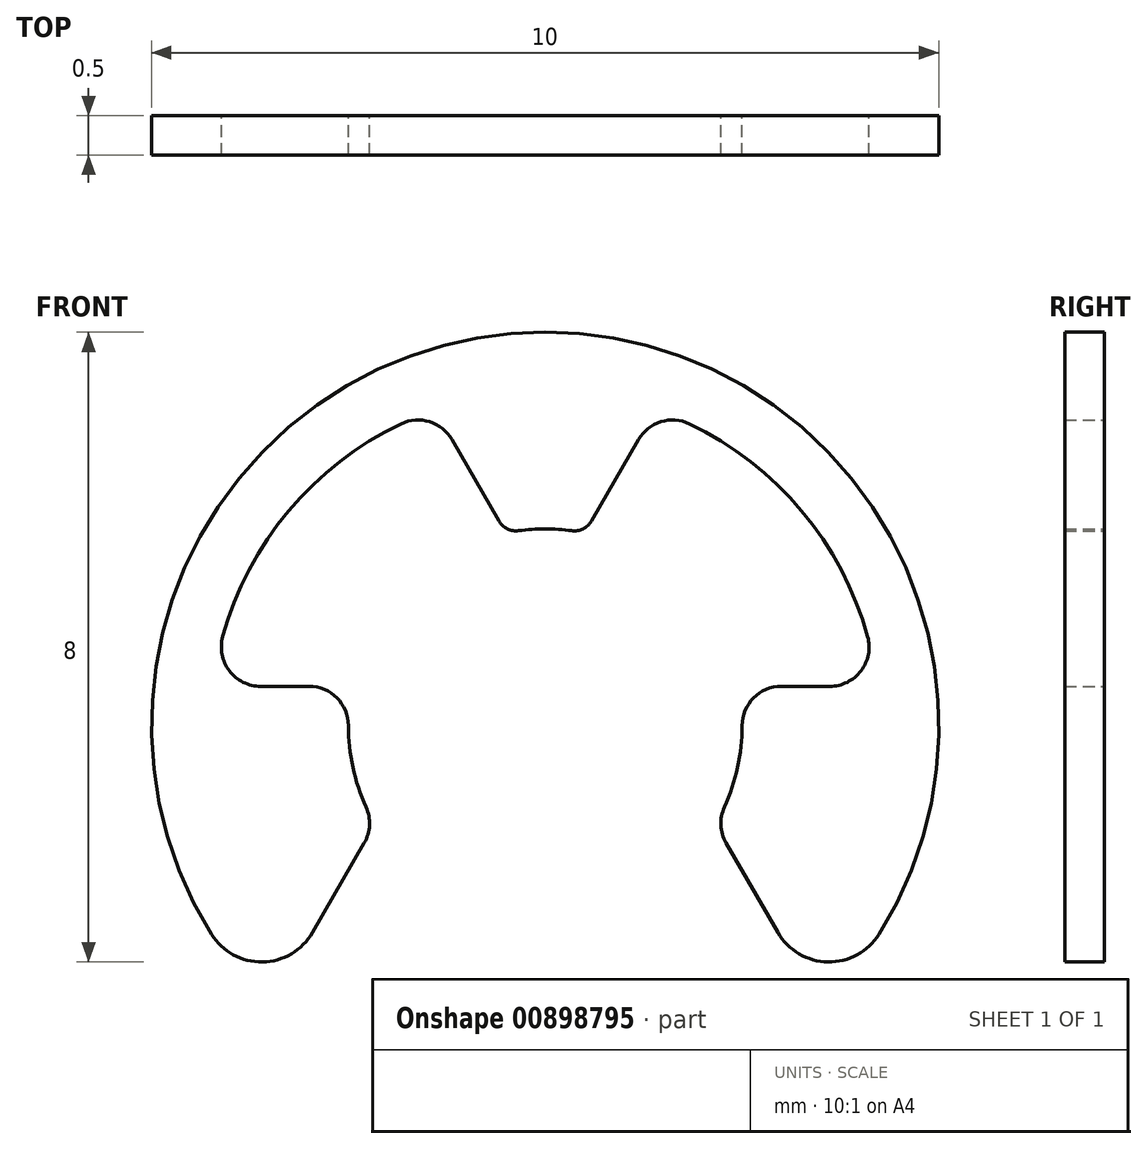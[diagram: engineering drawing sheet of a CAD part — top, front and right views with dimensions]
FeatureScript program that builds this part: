
annotation { "Feature Type Name" : "Feature", "Feature Type Description" : "" }
export const myFeature = defineFeature(function(context is Context, id is Id, definition is map)
    precondition{}
    {
        {
            var Q0;
            Q0=qCreatedBy(makeId("Front.planeOp"),FACE);
            var sketch = newSketch(context, id + "F0", { "sketchPlane" : qUnion([Q0])});
            skArc(sketch, "E0", {"start": v(4.24, -2.65) * mm, "mid": v(0, 5) * mm, "end": v(-4.24, -2.65) * mm});
            skArc(sketch, "E1", {"start": v(4.1, 1.13) * mm, "mid": v(3.26, 2.73) * mm, "end": v(1.83, 3.83) * mm});
            skArc(sketch, "E2", {"start": v(2.28, -1.03) * mm, "mid": v(2.44, -0.53) * mm, "end": v(2.5, 0) * mm});
            skLineSegment(sketch, "E3", {"start": v(-2.95, -2.63) * mm, "end": v(-2.3, -1.5) * mm});
            skLineSegment(sketch, "E4", {"start": v(2.95, -2.63) * mm, "end": v(2.3, -1.5) * mm});
            skLineSegment(sketch, "E5", {"start": v(3, 0.5) * mm, "end": v(3.61, 0.5) * mm});
            skLineSegment(sketch, "E6", {"start": v(-3, 0.5) * mm, "end": v(-3.61, 0.5) * mm});
            skLineSegment(sketch, "E7", {"start": v(-1.18, 3.63) * mm, "end": v(-0.59, 2.6) * mm});
            skLineSegment(sketch, "E8", {"start": v(0.59, 2.6) * mm, "end": v(1.18, 3.63) * mm});
            skArc(sketch, "E9.trimOffspring", {"start": v(-2.5, 0) * mm, "mid": v(-2.44, -0.53) * mm, "end": v(-2.28, -1.03) * mm});
            skArc(sketch, "E10.trimOffspring", {"start": v(0.34, 2.48) * mm, "mid": v(0, 2.5) * mm, "end": v(-0.34, 2.48) * mm});
            skArc(sketch, "E11.trimOffspring", {"start": v(-1.83, 3.83) * mm, "mid": v(-3.26, 2.73) * mm, "end": v(-4.1, 1.13) * mm});
            skPoint(sketch, "E12.visualSharp", {"position": v(-3.5, -3.57) * mm});
            skArc(sketch, "E12.filletArc", {"start": v(-4.24, -2.65) * mm, "mid": v(-3.6, -3) * mm, "end": v(-2.95, -2.63) * mm});
            skPoint(sketch, "E13.visualSharp", {"position": v(3.5, -3.57) * mm});
            skArc(sketch, "E13.filletArc", {"start": v(2.95, -2.63) * mm, "mid": v(3.6, -3) * mm, "end": v(4.24, -2.65) * mm});
            skPoint(sketch, "E14.visualSharp", {"position": v(4.22, 0.5) * mm});
            skArc(sketch, "E14.filletArc", {"start": v(3.61, 0.5) * mm, "mid": v(4.01, 0.7) * mm, "end": v(4.1, 1.13) * mm});
            skPoint(sketch, "E15.visualSharp", {"position": v(-4.22, 0.5) * mm});
            skArc(sketch, "E15.filletArc", {"start": v(-4.1, 1.13) * mm, "mid": v(-4.01, 0.7) * mm, "end": v(-3.61, 0.5) * mm});
            skPoint(sketch, "E16.visualSharp", {"position": v(-1.4, 4.01) * mm});
            skArc(sketch, "E16.filletArc", {"start": v(-1.18, 3.63) * mm, "mid": v(-1.47, 3.86) * mm, "end": v(-1.83, 3.83) * mm});
            skPoint(sketch, "E17.visualSharp", {"position": v(1.4, 4.01) * mm});
            skArc(sketch, "E17.filletArc", {"start": v(1.83, 3.83) * mm, "mid": v(1.47, 3.86) * mm, "end": v(1.18, 3.63) * mm});
            skPoint(sketch, "E18.visualSharp", {"position": v(2.16, -1.25) * mm});
            skArc(sketch, "E18.filletArc", {"start": v(2.28, -1.03) * mm, "mid": v(2.23, -1.26) * mm, "end": v(2.3, -1.5) * mm});
            skPoint(sketch, "E19.visualSharp", {"position": v(-2.16, -1.25) * mm});
            skArc(sketch, "E19.filletArc", {"start": v(-2.3, -1.5) * mm, "mid": v(-2.23, -1.26) * mm, "end": v(-2.28, -1.03) * mm});
            skPoint(sketch, "E20.visualSharp", {"position": v(2.45, 0.5) * mm});
            skArc(sketch, "E20.filletArc", {"start": v(3, 0.5) * mm, "mid": v(2.65, 0.35) * mm, "end": v(2.5, 0) * mm});
            skPoint(sketch, "E21.visualSharp", {"position": v(-2.45, 0.5) * mm});
            skArc(sketch, "E21.filletArc", {"start": v(-2.5, 0) * mm, "mid": v(-2.65, 0.35) * mm, "end": v(-3, 0.5) * mm});
            skPoint(sketch, "E22.visualSharp", {"position": v(0.5, 2.45) * mm});
            skArc(sketch, "E22.filletArc", {"start": v(0.34, 2.48) * mm, "mid": v(0.48, 2.5) * mm, "end": v(0.59, 2.6) * mm});
            skPoint(sketch, "E23.visualSharp", {"position": v(-0.5, 2.45) * mm});
            skArc(sketch, "E23.filletArc", {"start": v(-0.59, 2.6) * mm, "mid": v(-0.48, 2.5) * mm, "end": v(-0.34, 2.48) * mm});
            skSolve(sketch);
        }
        {
            var Q0;
            Q0 = qSketchRegion(id + "F0", true);
            extrude(context, id + "F1", {"entities" : qUnion([Q0]), "depth" : .5 * mm, "offsetDistance" : 25 * mm});
        }
    });
